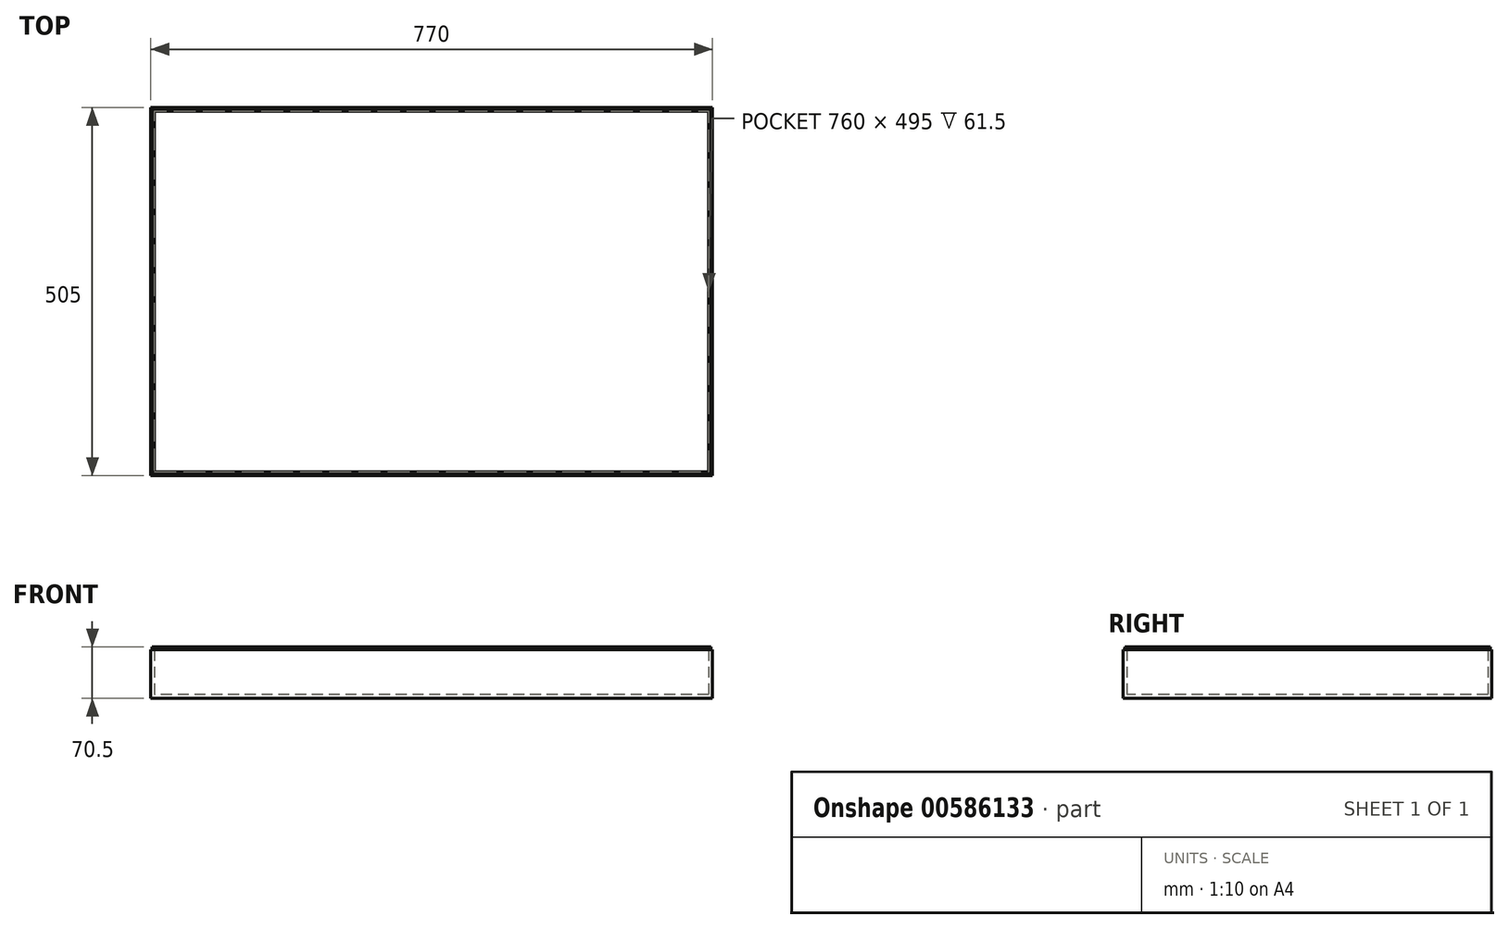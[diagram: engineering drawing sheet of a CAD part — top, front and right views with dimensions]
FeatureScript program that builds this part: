
annotation { "Feature Type Name" : "Feature", "Feature Type Description" : "" }
export const myFeature = defineFeature(function(context is Context, id is Id, definition is map)
    precondition{}
    {
        {
            var Q0;
            Q0=qCreatedBy(makeId("Top.planeOp"),FACE);
            var sketch = newSketch(context, id + "F0", { "sketchPlane" : qUnion([Q0])});
            skLineSegment(sketch, "E0.bottom", {"start": v(385, 252.5) * mm, "end": v(-385, 252.5) * mm});
            skLineSegment(sketch, "E0.top", {"start": v(385, -252.5) * mm, "end": v(-385, -252.5) * mm});
            skLineSegment(sketch, "E0.left", {"start": v(385, 252.5) * mm, "end": v(385, -252.5) * mm});
            skLineSegment(sketch, "E0.right", {"start": v(-385, 252.5) * mm, "end": v(-385, -252.5) * mm});
            skPoint(sketch, "E0.middle", {"position": v(0, 0) * mm});
            skSolve(sketch);
        }
        {
            var Q0;
            Q0=qSketchRegion(id+"F0",true);
            extrude(context, id + "F1", {"entities" : qUnion([Q0]), "depth" : 2 * mm, "offsetDistance" : 25.4 * mm, "hasSecondDirection" : true, "secondDirectionOppositeDirection" : true, "secondDirectionDepth" : 3 * mm});
        }
        {
            var Q0;
            Q0=makeQuery(id+"F1.opExtrude","CAP_FACE",FACE,{"disambiguationData":[OSD([sQuery(id+"F0.wireOp",EDGE,"E0.bottom"),sQuery(id+"F0.wireOp",EDGE,"E0.top"),sQuery(id+"F0.wireOp",EDGE,"E0.left"),sQuery(id+"F0.wireOp",EDGE,"E0.right")])],"isStart":false});
            var sketch = newSketch(context, id + "F2", { "sketchPlane" : qUnion([Q0])});
            skLineSegment(sketch, "E1.bottom", {"start": v(385, -252.5) * mm, "end": v(-385, -252.5) * mm});
            skLineSegment(sketch, "E1.top", {"start": v(385, 252.5) * mm, "end": v(-385, 252.5) * mm});
            skLineSegment(sketch, "E1.left", {"start": v(385, -252.5) * mm, "end": v(385, 252.5) * mm});
            skLineSegment(sketch, "E1.right", {"start": v(-385, -252.5) * mm, "end": v(-385, 252.5) * mm});
            skPoint(sketch, "E1.middle", {"position": v(0, 0) * mm});
            skLineSegment(sketch, "E2.bottom", {"start": v(-385, -252.5) * mm, "end": v(-380, -252.5) * mm});
            skLineSegment(sketch, "E2.left", {"start": v(-385, -252.5) * mm, "end": v(-385, -247.5) * mm});
            skLineSegment(sketch, "E3.bottom", {"start": v(385, 252.5) * mm, "end": v(380, 252.5) * mm});
            skLineSegment(sketch, "E3.left", {"start": v(385, 252.5) * mm, "end": v(385, 247.5) * mm});
            skLineSegment(sketch, "E4.bottom", {"start": v(380, 247.5) * mm, "end": v(-380, 247.5) * mm});
            skLineSegment(sketch, "E4.top", {"start": v(380, -247.5) * mm, "end": v(-380, -247.5) * mm});
            skLineSegment(sketch, "E4.left", {"start": v(380, 247.5) * mm, "end": v(380, -247.5) * mm});
            skLineSegment(sketch, "E4.right", {"start": v(-380, 247.5) * mm, "end": v(-380, -247.5) * mm});
            skSolve(sketch);
        }
        {
            var Q0;
            Q0=makeQuery(id+"F2.imprint","IMPRINT",FACE,{"disambiguationData":[TD([[makeQuery(id+"F2.imprint","IMPRINT",EDGE,{"derivedFrom":sQuery(id+"F2.wireOp",EDGE,"E1.bottom")}),-1.0]])]});
            extrude(context, id + "F3", {"entities" : qUnion([Q0]), "operationType" : NewBodyOperationType.ADD, "depth" : 63.5 * mm - 2 * mm, "offsetDistance" : 25.4 * mm});
        }
        {
            var Q0;
            Q0=makeQuery(id+"F3.opExtrude","CAP_FACE",FACE,{"disambiguationData":[OSD([sQuery(id+"F2.wireOp",EDGE,"E1.bottom"),sQuery(id+"F2.wireOp",EDGE,"E1.top"),sQuery(id+"F2.wireOp",EDGE,"E1.left"),sQuery(id+"F2.wireOp",EDGE,"E1.right"),sQuery(id+"F2.wireOp",EDGE,"E2.bottom"),sQuery(id+"F2.wireOp",EDGE,"E2.left"),sQuery(id+"F2.wireOp",EDGE,"E3.bottom"),sQuery(id+"F2.wireOp",EDGE,"E3.left"),sQuery(id+"F2.wireOp",EDGE,"E4.bottom"),sQuery(id+"F2.wireOp",EDGE,"E4.top"),sQuery(id+"F2.wireOp",EDGE,"E4.left"),sQuery(id+"F2.wireOp",EDGE,"E4.right")])],"isStart":false});
            var sketch = newSketch(context, id + "F4", { "sketchPlane" : qUnion([Q0])});
            skLineSegment(sketch, "E5.bottom", {"start": v(-380, -247.5) * mm, "end": v(-381, -247.5) * mm});
            skLineSegment(sketch, "E5.top", {"start": v(-380, -248.5) * mm, "end": v(-381, -248.5) * mm});
            skLineSegment(sketch, "E5.left", {"start": v(-380, -247.5) * mm, "end": v(-380, -248.5) * mm});
            skLineSegment(sketch, "E5.right", {"start": v(-381, -247.5) * mm, "end": v(-381, -248.5) * mm});
            skLineSegment(sketch, "E6.bottom", {"start": v(380, 247.5) * mm, "end": v(381, 247.5) * mm});
            skLineSegment(sketch, "E6.top", {"start": v(380, 248.5) * mm, "end": v(381, 248.5) * mm});
            skLineSegment(sketch, "E6.left", {"start": v(380, 247.5) * mm, "end": v(380, 248.5) * mm});
            skLineSegment(sketch, "E6.right", {"start": v(381, 247.5) * mm, "end": v(381, 248.5) * mm});
            skLineSegment(sketch, "E7.top", {"start": v(381, 250.5) * mm, "end": v(383, 250.5) * mm});
            skLineSegment(sketch, "E7.right", {"start": v(383, 248.5) * mm, "end": v(383, 250.5) * mm});
            skLineSegment(sketch, "E8.top", {"start": v(-276, -250.5) * mm, "end": v(-383, -250.5) * mm});
            skLineSegment(sketch, "E8.right", {"start": v(-383, -248.5) * mm, "end": v(-383, -250.5) * mm});
            skLineSegment(sketch, "E9.bottom", {"start": v(-381, -248.5) * mm, "end": v(381, -248.5) * mm});
            skLineSegment(sketch, "E9.top", {"start": v(-381, 248.5) * mm, "end": v(381, 248.5) * mm});
            skLineSegment(sketch, "E9.left", {"start": v(-381, -248.5) * mm, "end": v(-381, 248.5) * mm});
            skLineSegment(sketch, "E9.right", {"start": v(381, -248.5) * mm, "end": v(381, 248.5) * mm});
            skLineSegment(sketch, "E10.bottom", {"start": v(383, 250.5) * mm, "end": v(-383, 250.5) * mm});
            skLineSegment(sketch, "E10.top", {"start": v(383, -250.5) * mm, "end": v(-383, -250.5) * mm});
            skLineSegment(sketch, "E10.left", {"start": v(383, 250.5) * mm, "end": v(383, -250.5) * mm});
            skLineSegment(sketch, "E10.right", {"start": v(-383, 250.5) * mm, "end": v(-383, -250.5) * mm});
            skSolve(sketch);
        }
        {
            var Q0;
            Q0=qSketchRegion(id+"F4",true);
            extrude(context, id + "F5", {"entities" : qUnion([Q0]), "operationType" : NewBodyOperationType.ADD, "depth" : 4 * mm, "offsetDistance" : 25.4 * mm});
        }
        {
            var Q0;
            Q0=makeQuery(id+"F5.opExtrude","SWEPT_FACE",FACE,{"disambiguationData":[OSD([sQuery(id+"F4.wireOp",EDGE,"E10.top")])]});
            var sketch = newSketch(context, id + "F6", { "sketchPlane" : qUnion([Q0])});
            skLineSegment(sketch, "E11.left", {"start": v(-33.51, 66.5) * mm, "end": v(-33.51, 68.5) * mm});
            skLineSegment(sketch, "E11.right", {"start": v(33.51, 66.5) * mm, "end": v(33.51, 68.5) * mm});
            skPoint(sketch, "E11.middle", {"position": v(0, 67.5) * mm});
            skLineSegment(sketch, "E12.bottom", {"start": v(0, 67.5) * mm, "end": v(-1.5, 67.5) * mm});
            skLineSegment(sketch, "E13.bottom", {"start": v(-1.5, 67.5) * mm, "end": v(-4.5, 67.5) * mm});
            skLineSegment(sketch, "E14.bottom", {"start": v(0, 67.5) * mm, "end": v(1.5, 67.5) * mm});
            skLineSegment(sketch, "E15.bottom", {"start": v(1.5, 67.5) * mm, "end": v(4.5, 67.5) * mm});
            skArc(sketch, "E16", {"start": v(-5.5, 66.5) * mm, "mid": v(-4.5, 65.5) * mm, "end": v(-3.5, 66.5) * mm});
            skArc(sketch, "E17", {"start": v(-2.5, 66.5) * mm, "mid": v(-1.5, 65.5) * mm, "end": v(-0.5, 66.5) * mm});
            skArc(sketch, "E18", {"start": v(0.5, 66.5) * mm, "mid": v(1.5, 65.5) * mm, "end": v(2.5, 66.5) * mm});
            skArc(sketch, "E19", {"start": v(3.5, 66.5) * mm, "mid": v(4.5, 65.5) * mm, "end": v(5.5, 66.5) * mm});
            skLineSegment(sketch, "E20", {"start": v(-5.5, 66.5) * mm, "end": v(-5.5, 67.5) * mm});
            skLineSegment(sketch, "E21", {"start": v(-3.5, 66.5) * mm, "end": v(-3.5, 67.5) * mm});
            skLineSegment(sketch, "E22", {"start": v(-2.5, 66.5) * mm, "end": v(-2.5, 67.5) * mm});
            skLineSegment(sketch, "E23", {"start": v(-0.5, 66.5) * mm, "end": v(-0.5, 67.5) * mm});
            skLineSegment(sketch, "E24", {"start": v(0.5, 66.5) * mm, "end": v(0.5, 67.5) * mm});
            skLineSegment(sketch, "E25", {"start": v(2.5, 66.5) * mm, "end": v(2.5, 67.5) * mm});
            skLineSegment(sketch, "E26", {"start": v(3.5, 66.5) * mm, "end": v(3.5, 67.5) * mm});
            skLineSegment(sketch, "E27", {"start": v(5.5, 66.5) * mm, "end": v(5.5, 67.5) * mm});
            skLineSegment(sketch, "E28", {"start": v(-5.5, 67.5) * mm, "end": v(-4.5, 67.5) * mm});
            skSolve(sketch);
        }
        {
            var Q0;
            Q0=makeQuery(id+"F6.imprint","IMPRINT",FACE,{"disambiguationData":[TD([[makeQuery(id+"F6.imprint","IMPRINT",EDGE,{"derivedFrom":sQuery(id+"F6.wireOp",EDGE,"E19")}),1.0]])]});
            var Q1;
            Q1=makeQuery(id+"F6.imprint","IMPRINT",FACE,{"disambiguationData":[TD([[makeQuery(id+"F6.imprint","IMPRINT",EDGE,{"derivedFrom":sQuery(id+"F6.wireOp",EDGE,"E18")}),1.0]])]});
            var Q2;
            Q2=makeQuery(id+"F6.imprint","IMPRINT",FACE,{"disambiguationData":[TD([[makeQuery(id+"F6.imprint","IMPRINT",EDGE,{"derivedFrom":sQuery(id+"F6.wireOp",EDGE,"E16")}),1.0]])]});
            var Q3;
            Q3=makeQuery(id+"F6.imprint","IMPRINT",FACE,{"disambiguationData":[TD([[makeQuery(id+"F6.imprint","IMPRINT",EDGE,{"derivedFrom":sQuery(id+"F6.wireOp",EDGE,"E17")}),1.0]])]});
            extrude(context, id + "F7", {"entities" : qUnion([Q0, Q1, Q2, Q3]), "operationType" : NewBodyOperationType.REMOVE, "oppositeDirection" : true, "depth" : 25.4 * mm, "offsetDistance" : 25.4 * mm});
        }
    });
